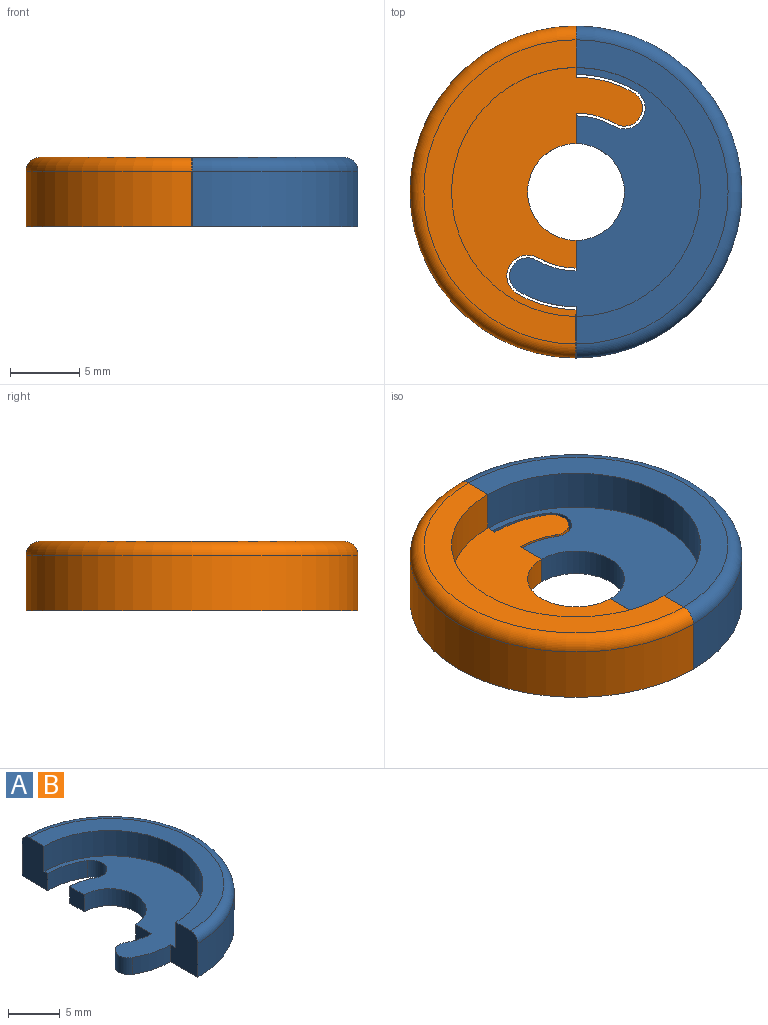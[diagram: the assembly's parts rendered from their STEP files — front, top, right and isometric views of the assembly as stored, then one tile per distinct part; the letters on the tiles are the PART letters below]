
ASSEMBLY  parts=2 mates=1
PART A: 17 faces, bbox 17.8x26x5 mm
  f0: plane 2.2x2mm, normal (-1,0,0), area 4.4mm2, adj f2,f3,f7,f14
  f1: plane 2x2mm, normal (-1,0,0), area 4mm2, adj f2,f3,f7,f11
  f2: plane 18x13.8mm, normal (0,0,1), area 105.6mm2, adj f0,f1,f6,f7,f8,f9,f11,f12
  f3: plane 24x16.8mm, normal (0,0,-1), area 204.6mm2, adj f0,f1,f4,f7,f8,f9,f11,f12
  f4: cylinder r=12mm len=24mm, axis (0,0,-1), area 150.8mm2, adj f3,f8,f9,f10
  f5: plane 22x11mm, normal (0,0,1), area 62.8mm2, adj f6,f8,f9,f10
  f6: cylinder r=9mm len=18mm, axis (0,0,-1), area 84.8mm2, adj f2,f5,f8,f9
  f7: cylinder r=3.5mm len=7mm, axis (0,0,-1), area 22mm2, adj f0,f1,f2,f3
  f8: plane 5x3.5mm, normal (-1,0,0), area 15.8mm2, adj f2,f3,f4,f5,f6,f10,f13
  f9: plane 5x3.7mm, normal (-1,0,0), area 16.2mm2, adj f2,f3,f4,f5,f6,f10,f16
  f10: torus R=11mm, axis (0,0,1), area 57.4mm2, adj f4,f5,f8,f9
  f11: cylinder r=5.5mm len=2.75mm, axis (0,0,1), area 5.8mm2, adj f1,f2,f3,f12
  f12: cylinder r=1.5mm len=2.8mm, axis (0,0,1), area 9.4mm2, adj f2,f3,f11,f13
  f13: cylinder r=8.5mm len=4.25mm, axis (0,0,1), area 8.9mm2, adj f2,f3,f8,f12
  f14: cylinder r=5.7mm len=2.85mm, axis (0,0,1), area 6mm2, adj f0,f2,f3,f15
  f15: cylinder r=1.3mm len=2.43mm, axis (0,0,1), area 8.2mm2, adj f2,f3,f14,f16
  f16: cylinder r=8.3mm len=4.15mm, axis (0,0,1), area 8.7mm2, adj f2,f3,f9,f15
PART B: same geometry as A
PLACE A t=(-11.12,-1.41,1.9)mm
PLACE B rot(axis=(0,0,1),180deg) t=(-11.12,-1.41,1.9)mm
MATE fastened B.f4 <-> A.f4  axis (0,0,-1) through (-11.12,-1.41,1.9)mm
